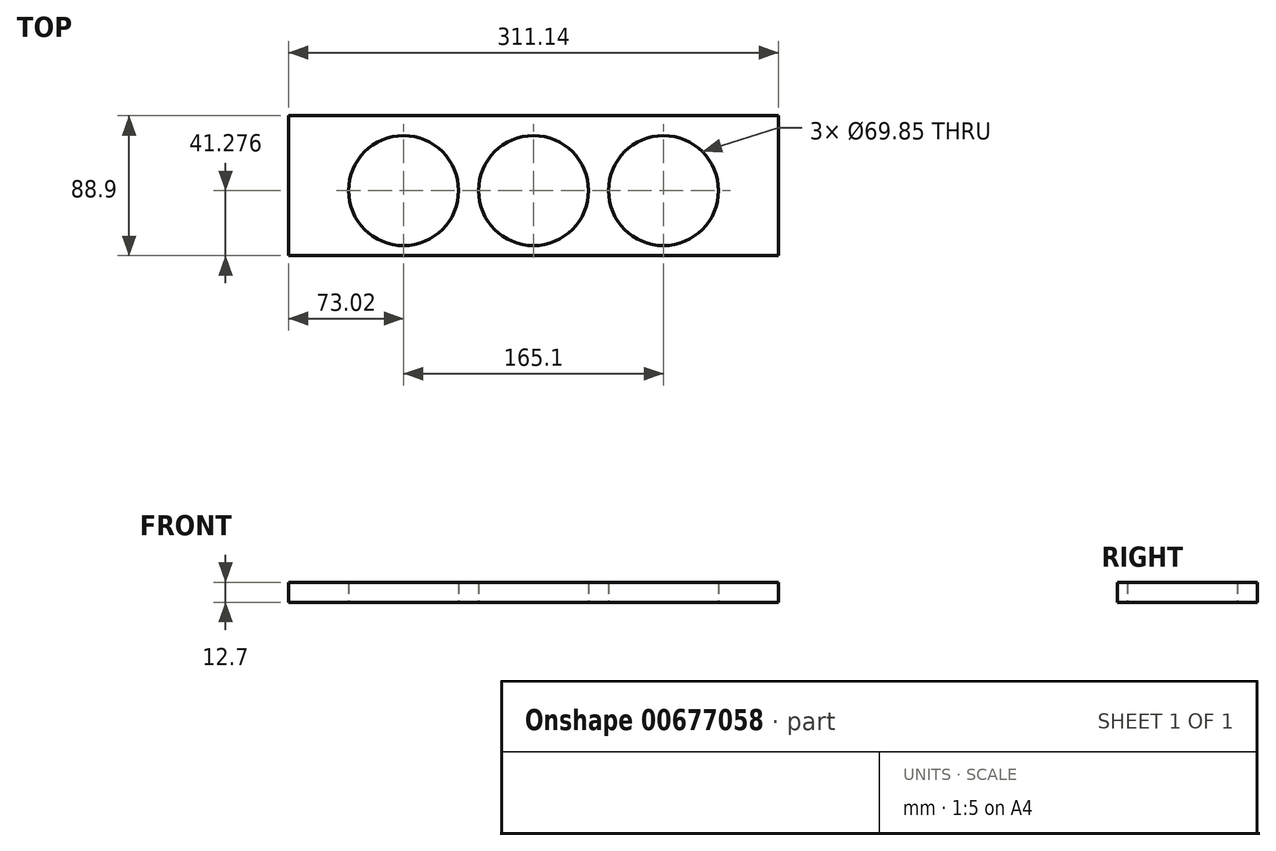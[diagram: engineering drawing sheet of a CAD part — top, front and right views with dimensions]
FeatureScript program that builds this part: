
annotation { "Feature Type Name" : "Feature", "Feature Type Description" : "" }
export const myFeature = defineFeature(function(context is Context, id is Id, definition is map)
    precondition{}
    {
        {
            var Q0;
            Q0=qCreatedBy(makeId("Top.planeOp"),FACE);
            var sketch = newSketch(context, id + "F0", { "sketchPlane" : qUnion([Q0])});
            skLineSegment(sketch, "E0.bottom", {"start": v(-155.58, -4.94) * mm, "end": v(155.58, -4.94) * mm});
            skLineSegment(sketch, "E0.top", {"start": v(-155.58, -93.84) * mm, "end": v(155.58, -93.84) * mm});
            skLineSegment(sketch, "E0.left", {"start": v(-155.58, -4.94) * mm, "end": v(-155.58, -93.84) * mm});
            skLineSegment(sketch, "E0.right", {"start": v(155.58, -4.94) * mm, "end": v(155.58, -93.84) * mm});
            skCircle(sketch, "E1", {"center": v(-82.55, -52.56) * mm, "radius": 34.93 * mm});
            skCircle(sketch, "E2", {"center": v(0, -52.56) * mm, "radius": 34.93 * mm});
            skCircle(sketch, "E3", {"center": v(82.55, -52.56) * mm, "radius": 34.93 * mm});
            skSolve(sketch);
        }
        {
            var Q0;
            Q0=makeQuery(id+"F0.imprint","IMPRINT",FACE,{"disambiguationData":[TD([[makeQuery(id+"F0.imprint","IMPRINT",EDGE,{"derivedFrom":sQuery(id+"F0.wireOp",EDGE,"E0.bottom")}),-1.0]])]});
            extrude(context, id + "F1", {"entities" : qUnion([Q0]), "depth" : 12.7 * mm, "offsetDistance" : 25.4 * mm});
        }
    });
